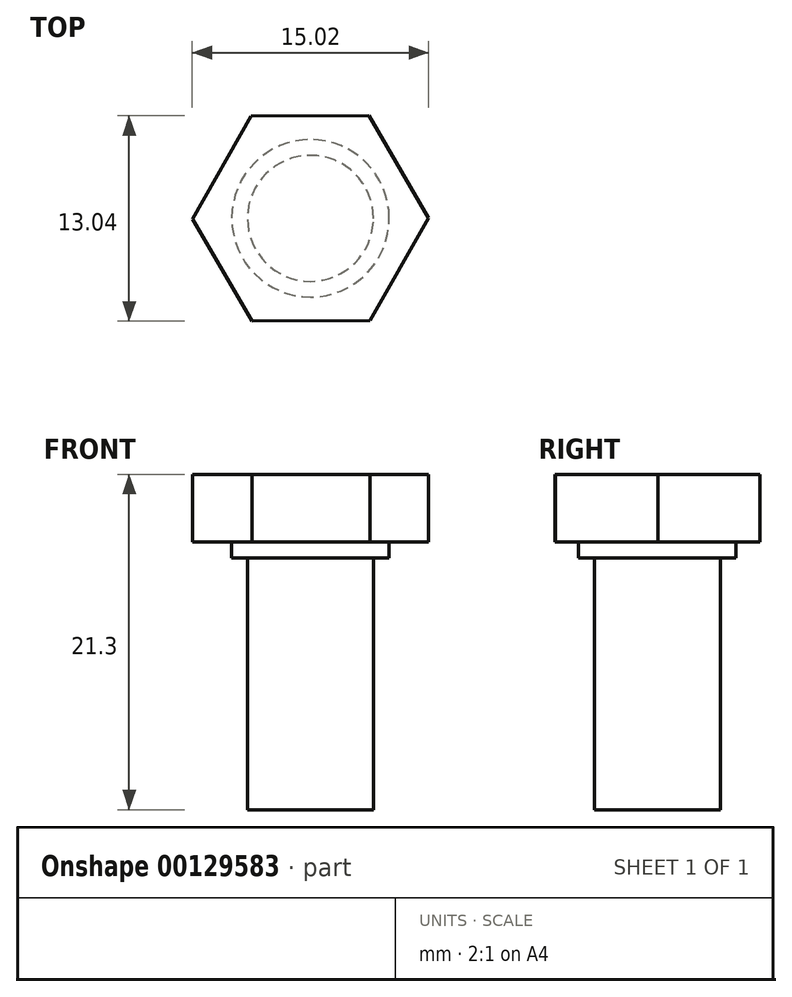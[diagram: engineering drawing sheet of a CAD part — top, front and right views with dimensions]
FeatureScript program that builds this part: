
annotation { "Feature Type Name" : "Feature", "Feature Type Description" : "" }
export const myFeature = defineFeature(function(context is Context, id is Id, definition is map)
    precondition{}
    {
        {
            var Q0;
            Q0=qCreatedBy(makeId("Top.planeOp"),FACE);
            var sketch = newSketch(context, id + "F0", { "sketchPlane" : qUnion([Q0])});
            skCircle(sketch, "E0", {"center": v(0, 0) * mm, "radius": 4 * mm});
            skSolve(sketch);
        }
        {
            var Q0;
            Q0=makeQuery(id+"F0.imprint","IMPRINT",FACE,{"disambiguationData":[TD([[makeQuery(id+"F0.imprint","IMPRINT",EDGE,{"derivedFrom":sQuery(id+"F0.wireOp",EDGE,"E0")}),1.0]])]});
            extrude(context, id + "F1", {"entities" : qUnion([Q0]), "depth" : 16 * mm});
        }
        {
            var Q0;
            Q0=makeQuery(id+"F1.opExtrude","CAP_FACE",FACE,{"disambiguationData":[OSD([sQuery(id+"F0.wireOp",EDGE,"E0")])],"isStart":false});
            var sketch = newSketch(context, id + "F2", { "sketchPlane" : qUnion([Q0])});
            skCircle(sketch, "E1.cCircle", {"center": v(0, 0) * mm, "radius": 6.5 * mm, "construction": true});
            skLineSegment(sketch, "E1.0", {"start": v(7.5, 0.03) * mm, "end": v(3.78, -6.48) * mm});
            skLineSegment(sketch, "E1.1", {"start": v(3.78, -6.48) * mm, "end": v(-3.72, -6.52) * mm});
            skLineSegment(sketch, "E1.2", {"start": v(-3.72, -6.52) * mm, "end": v(-7.5, -0.03) * mm});
            skLineSegment(sketch, "E1.3", {"start": v(-7.5, -0.03) * mm, "end": v(-3.78, 6.48) * mm});
            skLineSegment(sketch, "E1.4", {"start": v(-3.78, 6.48) * mm, "end": v(3.72, 6.52) * mm});
            skLineSegment(sketch, "E1.5", {"start": v(3.72, 6.52) * mm, "end": v(7.5, 0.03) * mm});
            skPoint(sketch, "E1.0.midPoint", {"position": v(5.64, -3.22) * mm});
            skSolve(sketch);
        }
        {
            var Q0;
            Q0 = qSketchRegion(id + "F2", true);
            extrude(context, id + "F3", {"entities" : qUnion([Q0]), "operationType" : NewBodyOperationType.ADD, "depth" : 5.3 * mm});
        }
        {
            var Q0;
            Q0=makeQuery(id+"F3.opExtrude","CAP_FACE",FACE,{"disambiguationData":[OSD([sQuery(id+"F2.wireOp",EDGE,"E1.0"),sQuery(id+"F2.wireOp",EDGE,"E1.1"),sQuery(id+"F2.wireOp",EDGE,"E1.2"),sQuery(id+"F2.wireOp",EDGE,"E1.3"),sQuery(id+"F2.wireOp",EDGE,"E1.4"),sQuery(id+"F2.wireOp",EDGE,"E1.5")])],"isStart":true});
            var sketch = newSketch(context, id + "F4", { "sketchPlane" : qUnion([Q0])});
            skCircle(sketch, "E2", {"center": v(0, 0) * mm, "radius": 5 * mm});
            skLineSegment(sketch, "E3.0", {"start": v(7.5, -0.03) * mm, "end": v(3.78, 6.48) * mm});
            skLineSegment(sketch, "E3.1", {"start": v(3.72, -6.52) * mm, "end": v(7.5, -0.03) * mm});
            skLineSegment(sketch, "E3.2", {"start": v(-3.78, -6.48) * mm, "end": v(3.72, -6.52) * mm});
            skLineSegment(sketch, "E3.3", {"start": v(-7.5, 0.03) * mm, "end": v(-3.78, -6.48) * mm});
            skLineSegment(sketch, "E3.4", {"start": v(-3.72, 6.52) * mm, "end": v(-7.5, 0.03) * mm});
            skLineSegment(sketch, "E3.5", {"start": v(3.78, 6.48) * mm, "end": v(-3.72, 6.52) * mm});
            skSolve(sketch);
        }
        {
            var Q0;
            Q0 = qSketchRegion(id + "F4", true);
            extrude(context, id + "F5", {"entities" : qUnion([Q0]), "operationType" : NewBodyOperationType.REMOVE, "oppositeDirection" : true, "depth" : 1 * mm});
        }
    });
